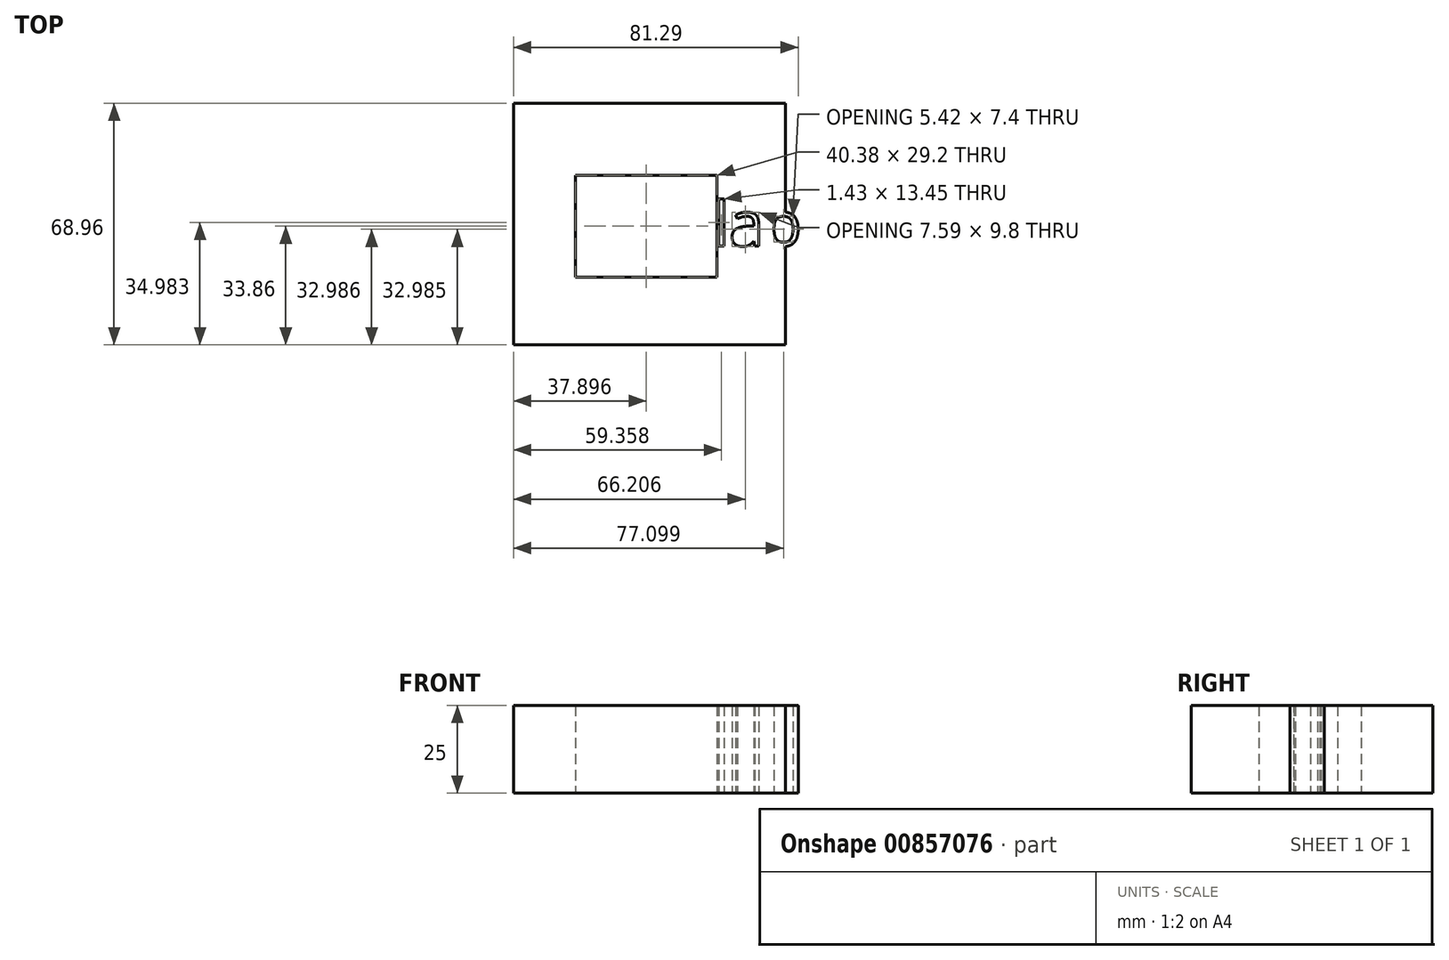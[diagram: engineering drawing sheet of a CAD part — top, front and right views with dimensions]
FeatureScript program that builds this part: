
annotation { "Feature Type Name" : "Feature", "Feature Type Description" : "" }
export const myFeature = defineFeature(function(context is Context, id is Id, definition is map)
    precondition{}
    {
        {
            var Q0;
            Q0=qCreatedBy(makeId("Top.planeOp"),FACE);
            var sketch = newSketch(context, id + "F0", { "sketchPlane" : qUnion([Q0])});
            skLineSegment(sketch, "E0.bottom", {"start": v(-37.43, 35.1) * mm, "end": v(40.23, 35.1) * mm});
            skLineSegment(sketch, "E0.top", {"start": v(-37.43, -33.86) * mm, "end": v(40.23, -33.86) * mm});
            skLineSegment(sketch, "E0.left", {"start": v(-37.43, 35.1) * mm, "end": v(-37.43, -33.86) * mm});
            skLineSegment(sketch, "E0.right", {"start": v(40.23, 35.1) * mm, "end": v(40.23, -33.86) * mm});
            skLineSegment(sketch, "E1.bottom", {"start": v(-19.73, 14.6) * mm, "end": v(20.66, 14.6) * mm});
            skLineSegment(sketch, "E1.top", {"start": v(-19.73, -14.6) * mm, "end": v(20.66, -14.6) * mm});
            skLineSegment(sketch, "E1.left", {"start": v(-19.73, 14.6) * mm, "end": v(-19.73, -14.6) * mm});
            skLineSegment(sketch, "E1.right", {"start": v(20.66, 14.6) * mm, "end": v(20.66, -14.6) * mm});
            skLineSegment(sketch, "E2", {"start": v(-19.73, 14.6) * mm, "end": v(-37.43, 35.1) * mm});
            skLineSegment(sketch, "E3", {"start": v(20.66, 14.6) * mm, "end": v(40.23, 35.1) * mm});
            skLineSegment(sketch, "E4", {"start": v(20.66, -14.6) * mm, "end": v(40.23, -33.86) * mm});
            skLineSegment(sketch, "E5", {"start": v(-19.73, -14.6) * mm, "end": v(-37.43, -33.86) * mm});
            skText(sketch, "E6", { "text": "fablab", "fontName": "OpenSans-Regular.ttf"});
            const initialGuessF0  = {"E6": [-0.00699, -0.0056, 1, 0, 0.01274]};
            skSetInitialGuess(sketch, initialGuessF0);
            skSolve(sketch);
        }
        {
            var Q0;
            Q0 = qSketchRegion(id + "F0", true);
            extrude(context, id + "F1", {"entities" : qUnion([Q0]), "depth" : 25 * mm, "offsetDistance" : 25 * mm});
        }
    });
